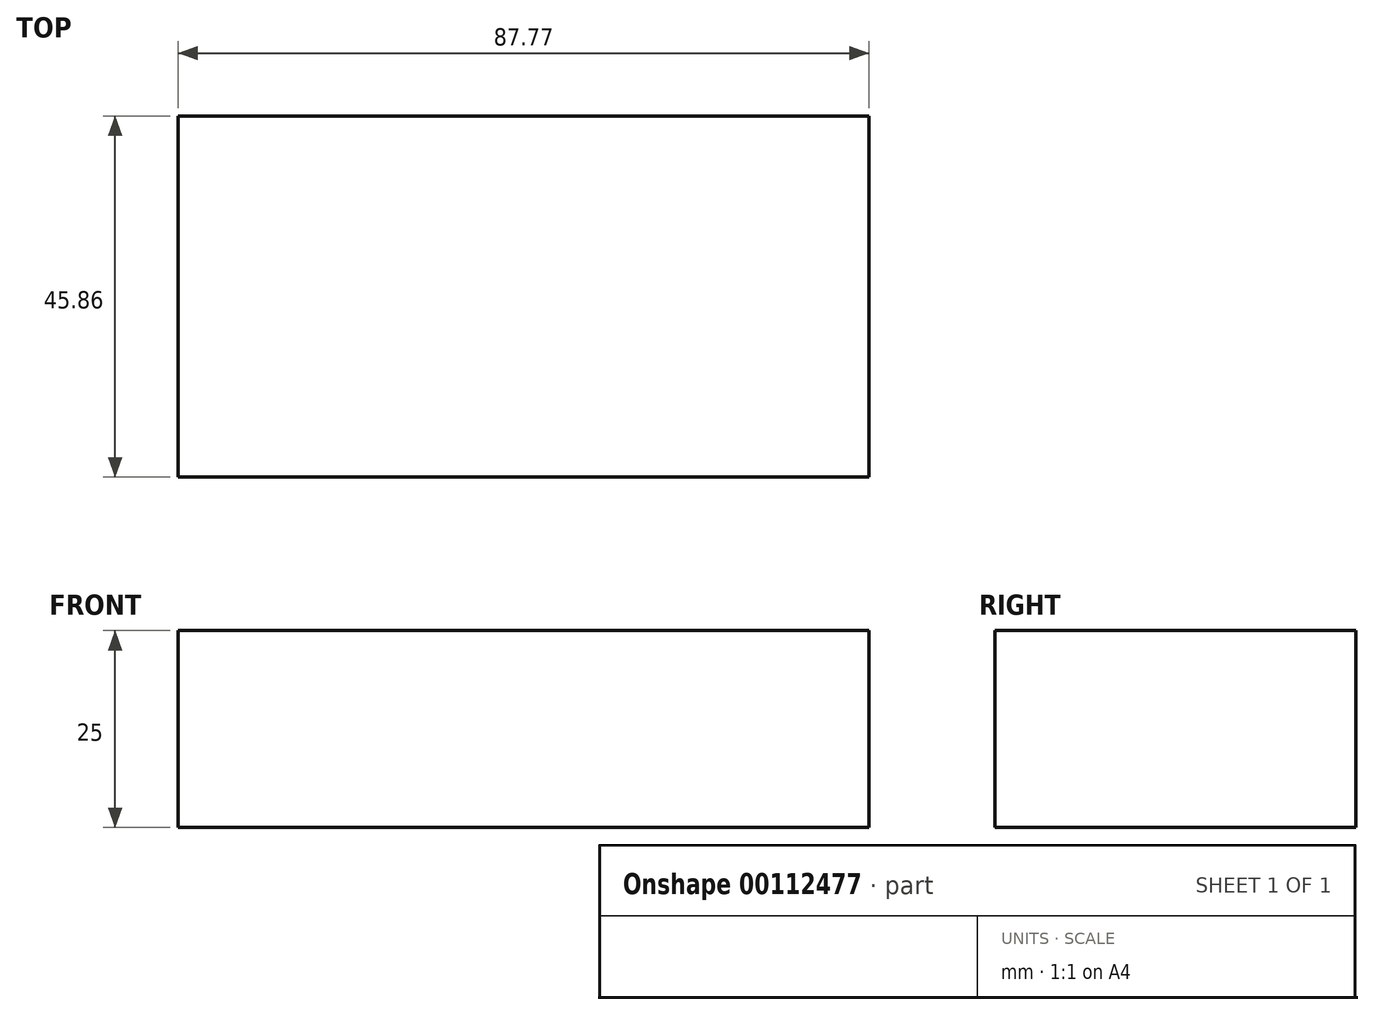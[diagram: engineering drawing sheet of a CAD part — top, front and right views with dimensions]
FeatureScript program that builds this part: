
annotation { "Feature Type Name" : "Feature", "Feature Type Description" : "" }
export const myFeature = defineFeature(function(context is Context, id is Id, definition is map)
    precondition{}
    {
        {
            var Q0;
            Q0=qCreatedBy(makeId("Top.planeOp"),FACE);
            var sketch = newSketch(context, id + "F0", { "sketchPlane" : qUnion([Q0])});
            skLineSegment(sketch, "E0.bottom", {"start": v(0, 0) * mm, "end": v(-87.77, 0) * mm});
            skLineSegment(sketch, "E0.top", {"start": v(0, 45.86) * mm, "end": v(-87.77, 45.86) * mm});
            skLineSegment(sketch, "E0.left", {"start": v(0, 0) * mm, "end": v(0, 45.86) * mm});
            skLineSegment(sketch, "E0.right", {"start": v(-87.77, 0) * mm, "end": v(-87.77, 45.86) * mm});
            skSolve(sketch);
        }
        {
            var Q0;
            Q0 = qSketchRegion(id + "F0", true);
            extrude(context, id + "F1", {"entities" : qUnion([Q0]), "depth" : 25 * mm});
        }
    });
